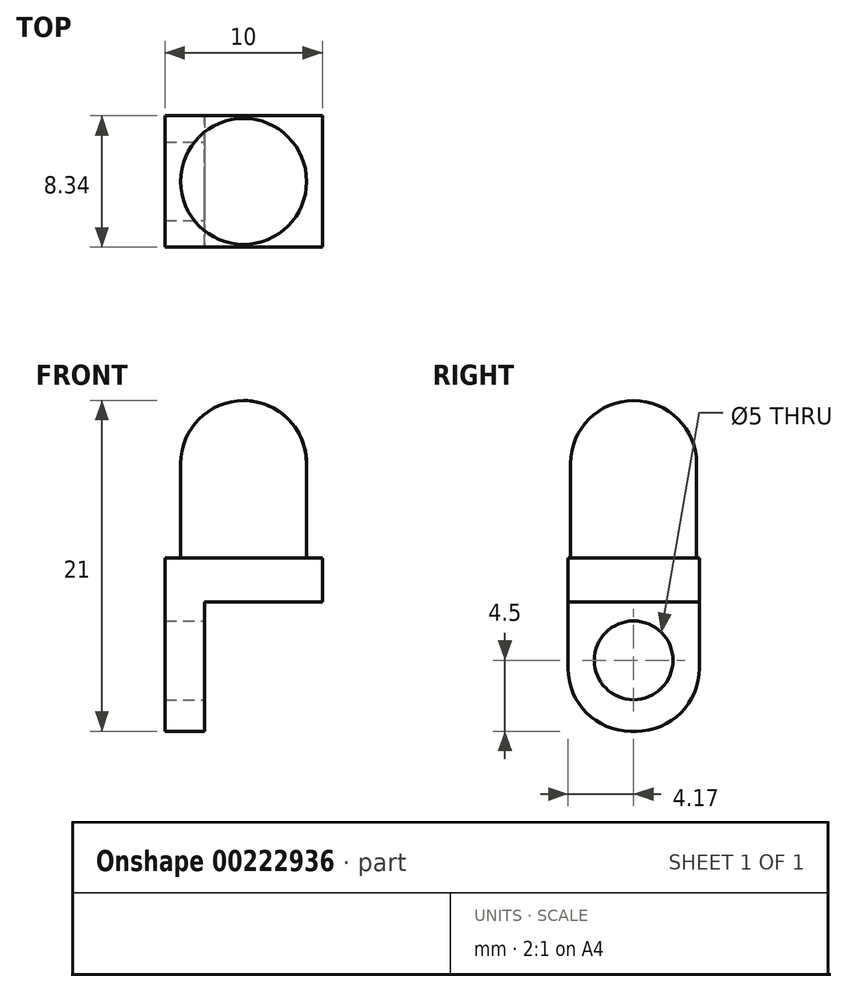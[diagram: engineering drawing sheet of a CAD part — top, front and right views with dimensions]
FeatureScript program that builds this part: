
annotation { "Feature Type Name" : "Feature", "Feature Type Description" : "" }
export const myFeature = defineFeature(function(context is Context, id is Id, definition is map)
    precondition{}
    {
        {
            var Q0;
            Q0=qCreatedBy(makeId("Front.planeOp"),FACE);
            var sketch = newSketch(context, id + "F0", { "sketchPlane" : qUnion([Q0])});
            skLineSegment(sketch, "E0.bottom", {"start": v(320.78, -573.92) * mm, "end": v(66.78, -573.92) * mm});
            skLineSegment(sketch, "E0.top", {"start": v(320.78, -319.92) * mm, "end": v(66.78, -319.92) * mm});
            skLineSegment(sketch, "E0.left", {"start": v(320.78, -573.92) * mm, "end": v(320.78, -319.92) * mm});
            skLineSegment(sketch, "E0.right", {"start": v(66.78, -573.92) * mm, "end": v(66.78, -319.92) * mm});
            skLineSegment(sketch, "E1.bottom", {"start": v(140.32, -506.6) * mm, "end": v(120.34, -506.6) * mm});
            skLineSegment(sketch, "E1.top", {"start": v(140.32, -426.14) * mm, "end": v(120.34, -426.14) * mm});
            skLineSegment(sketch, "E1.left", {"start": v(140.32, -506.6) * mm, "end": v(140.32, -426.14) * mm});
            skLineSegment(sketch, "E1.right", {"start": v(120.34, -506.6) * mm, "end": v(120.34, -426.14) * mm});
            skSolve(sketch);
        }
        {
            var Q0;
            Q0=makeQuery(id+"F0.imprint","IMPRINT",FACE,{"disambiguationData":[TD([[makeQuery(id+"F0.imprint","IMPRINT",EDGE,{"derivedFrom":sQuery(id+"F0.wireOp",EDGE,"E0.bottom")}),-1.0]])]});
            extrude(context, id + "F1", {"entities" : qUnion([Q0]), "depth" : 1 * mm});
        }
        {
            var Q0;
            Q0=makeQuery(id+"F1.opExtrude","SWEPT_BODY",BODY,{"disambiguationData":[OSD([sQuery(id+"F0.wireOp",EDGE,"E0.bottom"),sQuery(id+"F0.wireOp",EDGE,"E0.top"),sQuery(id+"F0.wireOp",EDGE,"E0.left"),sQuery(id+"F0.wireOp",EDGE,"E0.right"),sQuery(id+"F0.wireOp",EDGE,"E1.bottom"),sQuery(id+"F0.wireOp",EDGE,"E1.top"),sQuery(id+"F0.wireOp",EDGE,"E1.left"),sQuery(id+"F0.wireOp",EDGE,"E1.right")])]});
            deleteBodies(context, id + "F10", {"entities" : qUnion([Q0])});
        }
        {
            var Q0;
            Q0=qCreatedBy(makeId("Top.planeOp"),FACE);
            var sketch = newSketch(context, id + "F2", { "sketchPlane" : qUnion([Q0])});
            skLineSegment(sketch, "E2.bottom", {"start": v(5, 4.17) * mm, "end": v(-5, 4.17) * mm});
            skLineSegment(sketch, "E2.top", {"start": v(5, -4.17) * mm, "end": v(-5, -4.17) * mm});
            skLineSegment(sketch, "E2.left", {"start": v(5, 4.17) * mm, "end": v(5, -4.17) * mm});
            skLineSegment(sketch, "E2.right", {"start": v(-5, 4.17) * mm, "end": v(-5, -4.17) * mm});
            skPoint(sketch, "E2.middle", {"position": v(0, 0) * mm});
            skSolve(sketch);
        }
        {
            var Q0;
            Q0=makeQuery(id+"F2.imprint","IMPRINT",FACE,{"disambiguationData":[TD([[makeQuery(id+"F2.imprint","IMPRINT",EDGE,{"derivedFrom":sQuery(id+"F2.wireOp",EDGE,"E2.bottom")}),1.0]])]});
            extrude(context, id + "F3", {"entities" : qUnion([Q0]), "depth" : 16 * mm});
        }
        {
            var Q0;
            Q0=makeQuery(id+"F3.opExtrude","CAP_FACE",FACE,{"disambiguationData":[OSD([sQuery(id+"F2.wireOp",EDGE,"E2.bottom"),sQuery(id+"F2.wireOp",EDGE,"E2.top"),sQuery(id+"F2.wireOp",EDGE,"E2.left"),sQuery(id+"F2.wireOp",EDGE,"E2.right")])],"isStart":false});
            var sketch = newSketch(context, id + "F4", { "sketchPlane" : qUnion([Q0])});
            skCircle(sketch, "E3", {"center": v(0, 0) * mm, "radius": 4 * mm});
            skSolve(sketch);
        }
        {
            var Q0;
            Q0=makeQuery(id+"F4.imprint","IMPRINT",FACE,{"disambiguationData":[TD([[makeQuery(id+"F4.imprint","IMPRINT",EDGE,{"derivedFrom":sQuery(id+"F4.wireOp",EDGE,"E3")}),-1.0]])]});
            extrude(context, id + "F5", {"entities" : qUnion([Q0]), "operationType" : NewBodyOperationType.REMOVE, "oppositeDirection" : true, "depth" : 5 * mm});
        }
        {
            var Q0;
            Q0=makeQuery(id+"F3.opExtrude","SWEPT_FACE",FACE,{"disambiguationData":[OSD([sQuery(id+"F2.wireOp",EDGE,"E2.top")])]});
            var sketch = newSketch(context, id + "F6", { "sketchPlane" : qUnion([Q0])});
            skLineSegment(sketch, "E4.bottom", {"start": v(5, 0) * mm, "end": v(-2.48, 0) * mm});
            skLineSegment(sketch, "E4.top", {"start": v(5, 8.2) * mm, "end": v(-2.48, 8.2) * mm});
            skLineSegment(sketch, "E4.left", {"start": v(5, 0) * mm, "end": v(5, 8.2) * mm});
            skLineSegment(sketch, "E4.right", {"start": v(-2.48, 0) * mm, "end": v(-2.48, 8.2) * mm});
            skSolve(sketch);
        }
        {
            var Q0;
            Q0=makeQuery(id+"F6.imprint","IMPRINT",FACE,{"disambiguationData":[TD([[makeQuery(id+"F6.imprint","IMPRINT",EDGE,{"derivedFrom":sQuery(id+"F6.wireOp",EDGE,"E4.bottom")}),-1.0]])]});
            extrude(context, id + "F7", {"entities" : qUnion([Q0]), "operationType" : NewBodyOperationType.REMOVE, "oppositeDirection" : true, "depth" : 11 * mm});
        }
        {
            var Q0;
            Q0=makeQuery(id+"F3.opExtrude","CAP_FACE",FACE,{"disambiguationData":[OSD([sQuery(id+"F2.wireOp",EDGE,"E2.bottom"),sQuery(id+"F2.wireOp",EDGE,"E2.top"),sQuery(id+"F2.wireOp",EDGE,"E2.left"),sQuery(id+"F2.wireOp",EDGE,"E2.right")])],"isStart":false});
            extrude(context, id + "F8", {"entities" : qUnion([Q0]), "operationType" : NewBodyOperationType.ADD, "depth" : 5 * mm});
        }
        {
            var Q0;
            Q0=makeQuery(id+"F8.opExtrude","CAP_EDGE",EDGE,{"disambiguationData":[OSD([sQuery(id+"F4.wireOp",EDGE,"E3")])],"isStart":false});
            fillet(context, id + "F11", {"entities" : qUnion([Q0]), "radius" : 4 * mm, "tangentPropagation" : true, "allowEdgeOverflow" : false});
        }
        {
            var Q0;
            Q0=makeQuery(id+"F3.opExtrude","CAP_EDGE",EDGE,{"disambiguationData":[OSD([sQuery(id+"F2.wireOp",EDGE,"E2.top")])],"isStart":true});
            var Q1;
            Q1=makeQuery(id+"F3.opExtrude","CAP_EDGE",EDGE,{"disambiguationData":[OSD([sQuery(id+"F2.wireOp",EDGE,"E2.bottom")])],"isStart":true});
            fillet(context, id + "F12", {"entities" : qUnion([Q0, Q1]), "radius" : 4 * mm, "tangentPropagation" : true, "allowEdgeOverflow" : false});
        }
        {
            var Q0;
            Q0=makeQuery(id+"F7.boolean.opBoolean","COPY",FACE,{"derivedFrom":makeQuery(id+"F7.opExtrude","SWEPT_FACE",FACE,{"disambiguationData":[OSD([sQuery(id+"F6.wireOp",EDGE,"E4.right")])]})});
            var sketch = newSketch(context, id + "F9", { "sketchPlane" : qUnion([Q0])});
            skCircle(sketch, "E5", {"center": v(0, 4.5) * mm, "radius": 2.5 * mm});
            skSolve(sketch);
        }
        {
            var Q0;
            Q0=makeQuery(id+"F9.imprint","IMPRINT",FACE,{"disambiguationData":[TD([[makeQuery(id+"F9.imprint","IMPRINT",EDGE,{"derivedFrom":sQuery(id+"F9.wireOp",EDGE,"E5")}),1.0]])]});
            extrude(context, id + "F13", {"entities" : qUnion([Q0]), "operationType" : NewBodyOperationType.REMOVE, "oppositeDirection" : true, "depth" : 5 * mm});
        }
    });
